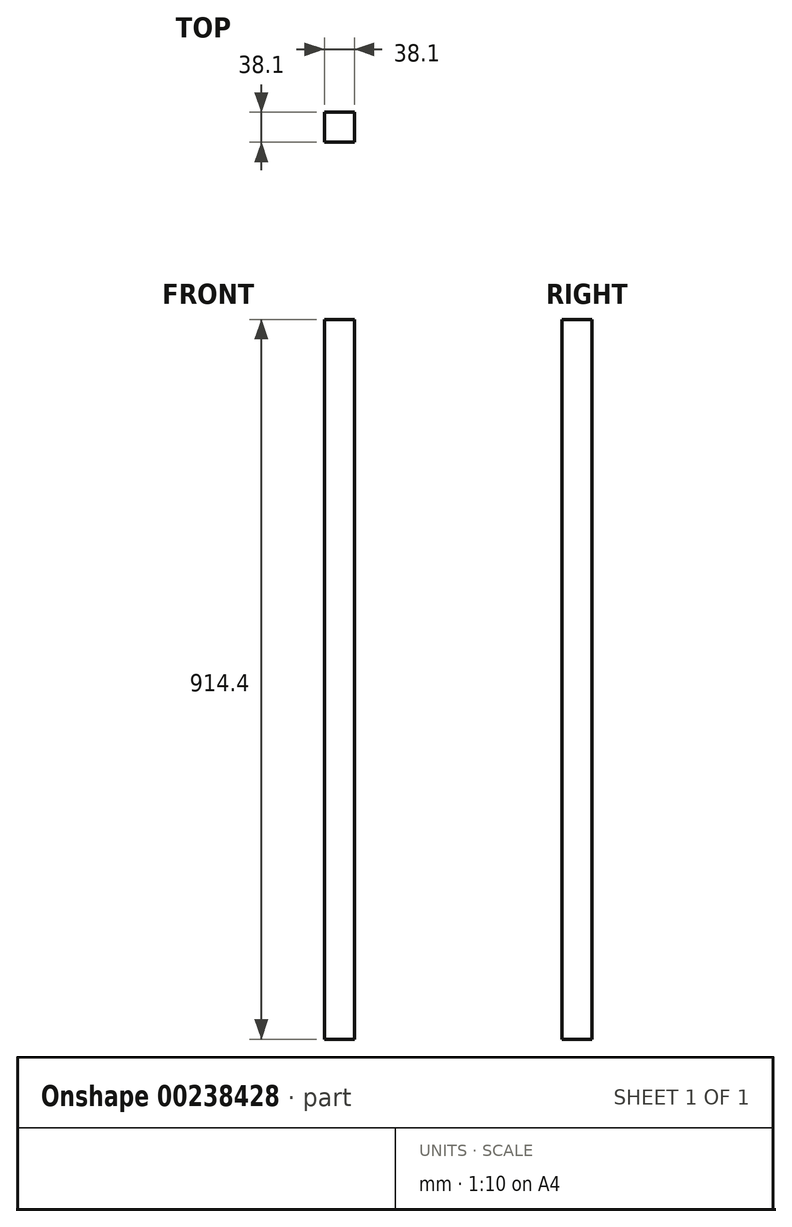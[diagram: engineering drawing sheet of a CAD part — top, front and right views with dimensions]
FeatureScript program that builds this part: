
annotation { "Feature Type Name" : "Feature", "Feature Type Description" : "" }
export const myFeature = defineFeature(function(context is Context, id is Id, definition is map)
    precondition{}
    {
        {
            var Q0;
            Q0=qCreatedBy(makeId("Top.planeOp"),FACE);
            var sketch = newSketch(context, id + "F0", { "sketchPlane" : qUnion([Q0])});
            skLineSegment(sketch, "E0.bottom", {"start": v(-60.52, 47.5) * mm, "end": v(-22.42, 47.5) * mm});
            skLineSegment(sketch, "E0.top", {"start": v(-60.52, 9.4) * mm, "end": v(-22.42, 9.4) * mm});
            skLineSegment(sketch, "E0.left", {"start": v(-60.52, 47.5) * mm, "end": v(-60.52, 9.4) * mm});
            skLineSegment(sketch, "E0.right", {"start": v(-22.42, 47.5) * mm, "end": v(-22.42, 9.4) * mm});
            skSolve(sketch);
        }
        {
            var Q0;
            Q0=makeQuery(id+"F0.imprint","IMPRINT",FACE,{"disambiguationData":[TD([[makeQuery(id+"F0.imprint","IMPRINT",EDGE,{"derivedFrom":sQuery(id+"F0.wireOp",EDGE,"E0.bottom")}),-1.0]])]});
            extrude(context, id + "F1", {"entities" : qUnion([Q0]), "depth" : 914.4 * mm});
        }
    });
